FCSTD DOCUMENT  (FreeCAD 0.19R24291 (Git))
Label: Problem06
License: All rights reserved
LicenseURL: http://en.wikipedia.org/wiki/All_rights_reserved
objects: App::FeaturePython×52, Part::Part2DObjectPython×46
note: 46 computed .brp shape members not serialized (recipe doc carries the construction recipe); baked Part::Feature solids carry a one-line shape summary decoded from their .brp

FEATURE [Part::Part2DObjectPython] Polygon  # Draft 2D object (typed FeaturePython)
  Area = 0
  ChamferSize = 0
  DrawMode = 0
  FacesNumber = 5
  FilletRadius = 0
  MakeFace = false
  Placement = pos=(-136.597,-39.2184,0) rot=(0,0,1;0.624663rad)
  Radius = 21.266
FEATURE [Part::Part2DObjectPython] Line004  # Draft 2D object (typed FeaturePython)
  Area = 0
  ChamferSize = 0
  Closed = false
  End = (-119.439,-51.781,0)
  FilletRadius = 0
  Length = 38.4706
  MakeFace = false
  Placement = pos=(-150.479,-29.0549,0) rot=(0,0,1;0rad)
  Points = (2) [(0,0,0),(31.0405,-22.7261,0)]
  Start = (-150.479,-29.0549,0)
  Subdivisions = 0
FEATURE [Part::Part2DObjectPython] Line005  # Draft 2D object (typed FeaturePython)
  Area = 0
  ChamferSize = 0
  Closed = false
  End = (-143.243,-59.4194,0)
  FilletRadius = 0
  Length = 38.4706
  MakeFace = false
  Placement = pos=(-131.221,-22.8754,0) rot=(0,0,1;0rad)
  Points = (2) [(0,0,0),(-12.0217,-36.544,0)]
  Start = (-131.221,-22.8754,0)
  Subdivisions = 0
FEATURE [Part::Part2DObjectPython] Line006  # Draft 2D object (typed FeaturePython)
  Area = 0
  ChamferSize = 0
  Closed = false
  End = (-136.597,-1.42e-14,0)
  FilletRadius = 0
  Length = 39.2184
  MakeFace = false
  Placement = pos=(-136.597,-39.2184,0) rot=(0,0,1;0rad)
  Points = (2) [(0,0,0),(0,39.2184,0)]
  Start = (-136.597,-39.2184,0)
  Subdivisions = 0
FEATURE [Part::Part2DObjectPython] Line007  # Draft 2D object (typed FeaturePython)
  Area = 0
  ChamferSize = 0
  Closed = false
  End = (-136.597,50,0)
  FilletRadius = 0
  Length = 50
  MakeFace = false
  Placement = pos=(-136.597,-1.42e-14,0) rot=(0,0,1;0rad)
  Points = (2) [(0,0,0),(-5.68434e-14,50,0)]
  Start = (-136.597,-1.42e-14,0)
  Subdivisions = 0
FEATURE [Part::Part2DObjectPython] Line009  # Draft 2D object (typed FeaturePython)
  Area = 0
  ChamferSize = 0
  Closed = false
  End = (-157.863,-2.13e-14,0)
  FilletRadius = 0
  Length = 39.1406
  MakeFace = false
  Placement = pos=(-157.863,-39.1406,0) rot=(0,0,1;0rad)
  Points = (2) [(0,0,0),(0,39.1406,0)]
  Start = (-157.863,-39.1406,0)
  Subdivisions = 0
FEATURE [Part::Part2DObjectPython] Line010  # Draft 2D object (typed FeaturePython)
  Area = 0
  ChamferSize = 0
  Closed = false
  End = (-119.347,-1.42e-14,0)
  FilletRadius = 0
  Length = 26.7815
  MakeFace = false
  Placement = pos=(-119.347,-26.7815,0) rot=(0,0,1;0rad)
  Points = (2) [(0,0,0),(0,26.7815,0)]
  Start = (-119.347,-26.7815,0)
  Subdivisions = 0
FEATURE [Part::Part2DObjectPython] Line011  # Draft 2D object (typed FeaturePython)
  Area = 0
  ChamferSize = 0
  Closed = false
  End = (-143.095,-1.78e-14,0)
  FilletRadius = 0
  Length = 18.9693
  MakeFace = false
  Placement = pos=(-143.095,-18.9693,0) rot=(0,0,1;0rad)
  Points = (2) [(0,0,0),(0,18.9693,0)]
  Start = (-143.095,-18.9693,0)
  Subdivisions = 0
FEATURE [Part::Part2DObjectPython] Line013  # Draft 2D object (typed FeaturePython)
  Area = 0
  ChamferSize = 0
  Closed = false
  End = (-157.863,50,0)
  FilletRadius = 0
  Length = 50
  MakeFace = false
  Placement = pos=(-157.863,-2.1e-14,0) rot=(0,0,1;0rad)
  Points = (2) [(0,0,0),(0,50,0)]
  Start = (-157.863,-2.1e-14,0)
  Subdivisions = 0
FEATURE [Part::Part2DObjectPython] Line014  # Draft 2D object (typed FeaturePython)
  Area = 0
  ChamferSize = 0
  Closed = false
  End = (-143.095,50,0)
  FilletRadius = 0
  Length = 50
  MakeFace = false
  Placement = pos=(-143.095,-1.78e-14,0) rot=(0,0,1;0rad)
  Points = (2) [(0,0,0),(-2.84217e-14,50,0)]
  Start = (-143.095,-1.78e-14,0)
  Subdivisions = 0
FEATURE [Part::Part2DObjectPython] Line015  # Draft 2D object (typed FeaturePython)
  Area = 0
  ChamferSize = 0
  Closed = false
  End = (-119.347,50,0)
  FilletRadius = 0
  Length = 50
  MakeFace = false
  Placement = pos=(-119.347,-1.42e-14,0) rot=(0,0,1;0rad)
  Points = (2) [(0,0,0),(-1.42109e-14,50,0)]
  Start = (-119.347,-1.42e-14,0)
  Subdivisions = 0
FEATURE [Part::Part2DObjectPython] Line016  # Draft 2D object (typed FeaturePython)
  Area = 0
  ChamferSize = 0
  Closed = false
  End = (-119.347,50,0)
  FilletRadius = 0
  Length = 38.516
  MakeFace = false
  Placement = pos=(-157.863,50,0) rot=(0,0,1;0rad)
  Points = (2) [(0,0,0),(38.516,0,0)]
  Start = (-157.863,50,0)
  Subdivisions = 0
FEATURE [Part::Part2DObjectPython] Line017  # Draft 2D object (typed FeaturePython)
  Area = 0
  ChamferSize = 0
  Closed = false
  End = (21.0287,62.5593,0)
  FilletRadius = 0
  Length = 50
  MakeFace = false
  Placement = pos=(-3.9713,19.258,0) rot=(0,0,-1;0.523599rad)
  Points = (2) [(0,0,0),(1.77636e-15,50,0)]
  Start = (-3.9713,19.258,0)
  Subdivisions = 0
FEATURE [Part::Part2DObjectPython] Line018  # Draft 2D object (typed FeaturePython)
  Area = 0
  ChamferSize = 0
  Closed = false
  End = (33.8184,55.1751,0)
  FilletRadius = 0
  Length = 50
  MakeFace = false
  Placement = pos=(8.81842,11.8739,0) rot=(0,0,-1;0.523599rad)
  Points = (2) [(0,0,0),(-2.39808e-14,50,0)]
  Start = (8.81842,11.8739,0)
  Subdivisions = 0
FEATURE [Part::Part2DObjectPython] Line019  # Draft 2D object (typed FeaturePython)
  Area = 0
  ChamferSize = 0
  Closed = false
  End = (39.4455,51.9263,0)
  FilletRadius = 0
  Length = 50
  MakeFace = false
  Placement = pos=(14.4455,8.62507,0) rot=(0,0,-1;0.523599rad)
  Points = (2) [(0,0,0),(-3.37508e-14,50,0)]
  Start = (14.4455,8.62507,0)
  Subdivisions = 0
FEATURE [Part::Part2DObjectPython] Line020  # Draft 2D object (typed FeaturePython)
  Area = 0
  ChamferSize = 0
  Closed = false
  End = (54.3845,43.3013,0)
  FilletRadius = 0
  Length = 50
  MakeFace = false
  Placement = pos=(29.3845,4e-15,0) rot=(0,0,-1;0.523599rad)
  Points = (2) [(0,0,0),(-2.13163e-14,50,0)]
  Start = (29.3845,4e-15,0)
  Subdivisions = 0
FEATURE [Part::Part2DObjectPython] Line021  # Draft 2D object (typed FeaturePython)
  Area = 0
  ChamferSize = 0
  Closed = false
  End = (54.3845,43.3013,0)
  FilletRadius = 0
  Length = 38.516
  MakeFace = false
  Placement = pos=(21.0287,62.5593,0) rot=(0,0,-1;0.523599rad)
  Points = (2) [(0,0,0),(38.516,-1.42109e-14,0)]
  Start = (21.0287,62.5593,0)
  Subdivisions = 0
FEATURE [Part::Part2DObjectPython] Line023  # Draft 2D object (typed FeaturePython)
  Area = 0
  ChamferSize = 0
  Closed = false
  End = (-3.9713,19.258,0)
  FilletRadius = 0
  Length = 58.3986
  MakeFace = false
  Placement = pos=(-3.9713,19.258,0) rot=(0,0,1;0rad)
  Points = (2) [(-1.24345e-14,-58.3986,0),(0,0,0)]
  Start = (-3.9713,-39.1406,0)
  Subdivisions = 0
FEATURE [Part::Part2DObjectPython] Line024  # Draft 2D object (typed FeaturePython)
  Area = 0
  ChamferSize = 0
  Closed = false
  End = (8.81842,11.8739,0)
  FilletRadius = 0
  Length = 71.2932
  MakeFace = false
  Placement = pos=(8.81842,11.8739,0) rot=(0,0,1;0rad)
  Points = (2) [(8.88178e-15,-71.2932,0),(0,0,0)]
  Start = (8.81842,-59.4194,0)
  Subdivisions = 0
FEATURE [App::FeaturePython] Text  # WARN: FeaturePython — macro-defined, semantics opaque (R4)
  Placement = pos=(-200.129,1.90969,0) rot=(0,0,1;0rad)
  Text = VP
FEATURE [App::FeaturePython] Text001  # WARN: FeaturePython — macro-defined, semantics opaque (R4)
  Placement = pos=(-200.407,-5.34313,0) rot=(0,0,1;0rad)
  Text = HP
FEATURE [App::FeaturePython] Dimension  # Draft dimension (typed FeaturePython)
  Diameter = false
  Dimline = (-169.104,5.51467,0)
  Direction = (0,0,0)
  Distance = 50
  End = (-157.863,-1.36e-14,0)
  Normal = (0,0,1)
  Start = (-157.863,50,0)
FEATURE [App::FeaturePython] Text002  # WARN: FeaturePython — macro-defined, semantics opaque (R4)
  Placement = pos=(-160.766,50.8523,0) rot=(0,0,1;0rad)
  Text = a'
FEATURE [App::FeaturePython] Text003  # WARN: FeaturePython — macro-defined, semantics opaque (R4)
  Placement = pos=(-162.087,-4.60433,0) rot=(0,0,1;0rad)
  Text = 1'
FEATURE [App::FeaturePython] Text004  # WARN: FeaturePython — macro-defined, semantics opaque (R4)
  Placement = pos=(-146.175,51.3734,0) rot=(0,0,1;0rad)
  Text = b'(e')
FEATURE [App::FeaturePython] Text005  # WARN: FeaturePython — macro-defined, semantics opaque (R4)
  Placement = pos=(-121.421,51.1129,0) rot=(0,0,1;0rad)
  Text = c'(d')
FEATURE [App::FeaturePython] Text006  # WARN: FeaturePython — macro-defined, semantics opaque (R4)
  Placement = pos=(-147.477,-4.90778,0) rot=(0,0,1;0rad)
  Text = 2'(5')
FEATURE [App::FeaturePython] Text007  # WARN: FeaturePython — macro-defined, semantics opaque (R4)
  Placement = pos=(-123.506,-4.64722,0) rot=(0,0,1;0rad)
  Text = 3'(4')
FEATURE [App::FeaturePython] Text008  # WARN: FeaturePython — macro-defined, semantics opaque (R4)
  Placement = pos=(-167.801,-38.7807,0) rot=(0,0,1;0rad)
  Text = a(1)
FEATURE [App::FeaturePython] Text009  # WARN: FeaturePython — macro-defined, semantics opaque (R4)
  Placement = pos=(-143.83,-65.0974,0) rot=(0,0,1;0rad)
  Text = b(2)
FEATURE [App::FeaturePython] Text010  # WARN: FeaturePython — macro-defined, semantics opaque (R4)
  Placement = pos=(-118.555,-50.7665,0) rot=(0,0,1;0rad)
  Text = c(3)
FEATURE [App::FeaturePython] Text011  # WARN: FeaturePython — macro-defined, semantics opaque (R4)
  Placement = pos=(-117.513,-25.7527,0) rot=(0,0,1;0rad)
  Text = d(4)
FEATURE [App::FeaturePython] Text012  # WARN: FeaturePython — macro-defined, semantics opaque (R4)
  Placement = pos=(-142.787,-17.4147,0) rot=(0,0,1;0rad)
  Text = e(5)
FEATURE [App::FeaturePython] Dimension001  # Draft dimension (typed FeaturePython)
  Diameter = false
  Dimline = (-151.386,-63.0129,0)
  Direction = (0,0,0)
  Distance = 24.9997
  End = (-143.243,-59.4194,0)
  Normal = (0,0,1)
  Start = (-157.863,-39.1406,0)
FEATURE [Part::Part2DObjectPython] Line027  # Draft 2D object (typed FeaturePython)
  Area = 0
  ChamferSize = 0
  Closed = false
  End = (-143.095,-18.9693,0)
  FilletRadius = 0
  Length = 223.348
  MakeFace = false
  Placement = pos=(-143.095,-18.9693,0) rot=(0,0,1;0rad)
  Points = (2) [(223.348,-2.4869e-14,0),(0,0,0)]
  Start = (80.253,-18.9693,0)
  Subdivisions = 0
FEATURE [Part::Part2DObjectPython] Line028  # Draft 2D object (typed FeaturePython)
  Area = 0
  ChamferSize = 0
  Closed = false
  End = (-157.863,-39.1406,0)
  FilletRadius = 0
  Length = 238.116
  MakeFace = false
  Placement = pos=(-157.863,-39.1406,0) rot=(0,0,1;0rad)
  Points = (2) [(238.116,-3.55271e-14,0),(0,0,0)]
  Start = (80.253,-39.1406,0)
  Subdivisions = 0
FEATURE [Part::Part2DObjectPython] Line029  # Draft 2D object (typed FeaturePython)
  Area = 0
  ChamferSize = 0
  Closed = false
  End = (-143.243,-59.4194,0)
  FilletRadius = 0
  Length = 223.496
  MakeFace = false
  Placement = pos=(-143.243,-59.4194,0) rot=(0,0,1;0rad)
  Points = (2) [(223.496,-4.26326e-14,0),(0,0,0)]
  Start = (80.253,-59.4194,0)
  Subdivisions = 0
FEATURE [Part::Part2DObjectPython] Line030  # Draft 2D object (typed FeaturePython)
  Area = 0
  ChamferSize = 0
  Closed = false
  End = (-119.347,-26.7815,0)
  FilletRadius = 0
  Length = 199.6
  MakeFace = false
  Placement = pos=(-119.347,-26.7815,0) rot=(0,0,1;0rad)
  Points = (2) [(199.6,-7.10543e-15,0),(0,0,0)]
  Start = (80.253,-26.7815,0)
  Subdivisions = 0
FEATURE [Part::Part2DObjectPython] Line031  # Draft 2D object (typed FeaturePython)
  Area = 0
  ChamferSize = 0
  Closed = false
  End = (-119.439,-51.781,0)
  FilletRadius = 0
  Length = 199.692
  MakeFace = false
  Placement = pos=(-119.439,-51.781,0) rot=(0,0,1;0rad)
  Points = (2) [(199.692,-6.39488e-14,0),(0,0,0)]
  Start = (80.253,-51.781,0)
  Subdivisions = 0
FEATURE [Part::Part2DObjectPython] Line032  # Draft 2D object (typed FeaturePython)
  Area = 0
  ChamferSize = 0
  Closed = false
  End = (21.0287,62.5593,0)
  FilletRadius = 0
  Length = 101.7
  MakeFace = false
  Placement = pos=(21.0287,62.5593,0) rot=(0,0,1;0rad)
  Points = (2) [(-1.06581e-14,-101.7,0),(0,0,0)]
  Start = (21.0287,-39.1406,0)
  Subdivisions = 0
FEATURE [Part::Part2DObjectPython] Line033  # Draft 2D object (typed FeaturePython)
  Area = 0
  ChamferSize = 0
  Closed = false
  End = (33.8184,55.1751,0)
  FilletRadius = 0
  Length = 114.594
  MakeFace = false
  Placement = pos=(33.8184,55.1751,0) rot=(0,0,1;0rad)
  Points = (2) [(0,-114.594,0),(0,0,0)]
  Start = (33.8184,-59.4194,0)
  Subdivisions = 0
FEATURE [App::FeaturePython] Text013  # WARN: FeaturePython — macro-defined, semantics opaque (R4)
  Placement = pos=(-7.59819,-37.5917,0) rot=(0,0,1;0rad)
  Text = 1
FEATURE [App::FeaturePython] Text014  # WARN: FeaturePython — macro-defined, semantics opaque (R4)
  Placement = pos=(-5.71338,-38.0629,0) rot=(0,0,1;0rad)
  Text = 1
FEATURE [App::FeaturePython] Text015  # WARN: FeaturePython — macro-defined, semantics opaque (R4)
  Placement = pos=(4.02486,-17.9582,0) rot=(0,0,1;0rad)
  Text = 5
FEATURE [App::FeaturePython] Text016  # WARN: FeaturePython — macro-defined, semantics opaque (R4)
  Placement = pos=(19.2582,-42.6379,0) rot=(0,0,1;0rad)
  Text = a
FEATURE [App::FeaturePython] Text017  # WARN: FeaturePython — macro-defined, semantics opaque (R4)
  Placement = pos=(9.52225,-64.1363,0) rot=(0,0,1;0rad)
  Text = 2
FEATURE [App::FeaturePython] Text018  # WARN: FeaturePython — macro-defined, semantics opaque (R4)
  Placement = pos=(29.9411,-30.5237,0) rot=(0,0,1;0rad)
  Text = 4
FEATURE [App::FeaturePython] Text019  # WARN: FeaturePython — macro-defined, semantics opaque (R4)
  Placement = pos=(29.1558,-49.8431,0) rot=(0,0,1;0rad)
  Text = 3
FEATURE [App::FeaturePython] Text020  # WARN: FeaturePython — macro-defined, semantics opaque (R4)
  Placement = pos=(6.53796,-17.9582,0) rot=(0,0,1;0rad)
  Text = 1
FEATURE [App::FeaturePython] Text021  # WARN: FeaturePython — macro-defined, semantics opaque (R4)
  Placement = pos=(32.2972,-31.309,0) rot=(0,0,1;0rad)
  Text = 1
FEATURE [App::FeaturePython] Text022  # WARN: FeaturePython — macro-defined, semantics opaque (R4)
  Placement = pos=(31.8269,-50.0418,0) rot=(0,0,1;0rad)
  Text = 1
FEATURE [App::FeaturePython] Text023  # WARN: FeaturePython — macro-defined, semantics opaque (R4)
  Placement = pos=(12.9787,-64.4921,0) rot=(0,0,1;0rad)
  Text = 1
FEATURE [App::FeaturePython] Text024  # WARN: FeaturePython — macro-defined, semantics opaque (R4)
  Placement = pos=(55.3862,-30.2235,0) rot=(0,0,1;0rad)
  Text = d
FEATURE [App::FeaturePython] Text025  # WARN: FeaturePython — macro-defined, semantics opaque (R4)
  Placement = pos=(55.2291,-50.6423,0) rot=(0,0,1;0rad)
  Text = c
FEATURE [App::FeaturePython] Text026  # WARN: FeaturePython — macro-defined, semantics opaque (R4)
  Placement = pos=(34.9729,-17.9378,0) rot=(0,0,1;0rad)
  Text = e
FEATURE [App::FeaturePython] Text027  # WARN: FeaturePython — macro-defined, semantics opaque (R4)
  Placement = pos=(34.6588,-62.8593,0) rot=(0,0,1;0rad)
  Text = b
FEATURE [App::FeaturePython] Text028  # WARN: FeaturePython — macro-defined, semantics opaque (R4)
  Placement = pos=(37.3233,-18.2723,0) rot=(0,0,1;0rad)
  Text = 1
FEATURE [App::FeaturePython] Text029  # WARN: FeaturePython — macro-defined, semantics opaque (R4)
  Placement = pos=(58.0564,-30.9949,0) rot=(0,0,1;0rad)
  Text = 1
FEATURE [App::FeaturePython] Text030  # WARN: FeaturePython — macro-defined, semantics opaque (R4)
  Placement = pos=(57.7422,-51.2567,0) rot=(0,0,1;0rad)
  Text = 1
FEATURE [Part::Part2DObjectPython] Line036  # Draft 2D object (typed FeaturePython)
  Area = 0
  ChamferSize = 0
  Closed = false
  End = (8.81842,-18.9693,0)
  FilletRadius = 0
  Length = 23.8843
  MakeFace = false
  Placement = pos=(-3.9713,-39.1406,0) rot=(0,0,1;0rad)
  Points = (2) [(0,0,0),(12.7897,20.1713,0)]
  Start = (-3.9713,-39.1406,0)
  Subdivisions = 0
FEATURE [Part::Part2DObjectPython] Line037  # Draft 2D object (typed FeaturePython)
  Area = 0
  ChamferSize = 0
  Closed = false
  End = (8.81842,-59.4194,0)
  FilletRadius = 0
  Length = 23.9751
  MakeFace = false
  Placement = pos=(-3.9713,-39.1406,0) rot=(0,0,1;0rad)
  Points = (2) [(0,0,0),(12.7897,-20.2788,0)]
  Start = (-3.9713,-39.1406,0)
  Subdivisions = 0
FEATURE [Part::Part2DObjectPython] Line038  # Draft 2D object (typed FeaturePython)
  Area = 0
  ChamferSize = 0
  Closed = false
  End = (29.3845,-59.4194,0)
  FilletRadius = 0
  Length = 59.4194
  MakeFace = false
  Placement = pos=(29.3845,7.1e-15,0) rot=(0,0,1;0rad)
  Points = (2) [(0,0,0),(-1.42109e-14,-59.4194,0)]
  Start = (29.3845,7.1e-15,0)
  Subdivisions = 0
FEATURE [Part::Part2DObjectPython] Line039  # Draft 2D object (typed FeaturePython)
  Area = 0
  ChamferSize = 0
  Closed = false
  End = (29.3845,-26.7815,0)
  FilletRadius = 0
  Length = 21.9999
  MakeFace = false
  Placement = pos=(8.81842,-18.9693,0) rot=(0,0,1;0rad)
  Points = (2) [(0,0,0),(20.5661,-7.8122,0)]
  Start = (8.81842,-18.9693,0)
  Subdivisions = 0
FEATURE [Part::Part2DObjectPython] Line040  # Draft 2D object (typed FeaturePython)
  Area = 0
  ChamferSize = 0
  Closed = false
  End = (29.3845,-51.781,0)
  FilletRadius = 0
  Length = 21.9388
  MakeFace = false
  Placement = pos=(8.81842,-59.4194,0) rot=(0,0,1;0rad)
  Points = (2) [(0,0,0),(20.5661,7.63835,0)]
  Start = (8.81842,-59.4194,0)
  Subdivisions = 0
FEATURE [Part::Part2DObjectPython] Line041  # Draft 2D object (typed FeaturePython)
  Area = 0
  ChamferSize = 0
  Closed = false
  End = (29.3845,-51.781,0)
  FilletRadius = 0
  Length = 24.9995
  MakeFace = false
  Placement = pos=(29.3845,-26.7815,0) rot=(0,0,1;0rad)
  Points = (2) [(0,0,0),(0,-24.9995,0)]
  Start = (29.3845,-26.7815,0)
  Subdivisions = 0
FEATURE [Part::Part2DObjectPython] Line042  # Draft 2D object (typed FeaturePython)
  Area = 0
  ChamferSize = 0
  Closed = false
  End = (54.3845,-51.781,0)
  FilletRadius = 0
  Length = 21.9388
  MakeFace = false
  Placement = pos=(33.8184,-59.4194,0) rot=(0,0,1;0rad)
  Points = (2) [(0,0,0),(20.5661,7.63835,0)]
  Start = (33.8184,-59.4194,0)
  Subdivisions = 0
FEATURE [Part::Part2DObjectPython] Line043  # Draft 2D object (typed FeaturePython)
  Area = 0
  ChamferSize = 0
  Closed = false
  End = (33.8184,-59.4194,0)
  FilletRadius = 0
  Length = 23.9751
  MakeFace = false
  Placement = pos=(21.0287,-39.1406,0) rot=(0,0,1;0rad)
  Points = (2) [(0,0,0),(12.7897,-20.2788,0)]
  Start = (21.0287,-39.1406,0)
  Subdivisions = 0
FEATURE [Part::Part2DObjectPython] Line044  # Draft 2D object (typed FeaturePython)
  Area = 0
  ChamferSize = 0
  Closed = false
  End = (33.8184,-18.9693,0)
  FilletRadius = 0
  Length = 23.8843
  MakeFace = false
  Placement = pos=(21.0287,-39.1406,0) rot=(0,0,1;0rad)
  Points = (2) [(0,0,0),(12.7897,20.1713,0)]
  Start = (21.0287,-39.1406,0)
  Subdivisions = 0
FEATURE [Part::Part2DObjectPython] Line045  # Draft 2D object (typed FeaturePython)
  Area = 0
  ChamferSize = 0
  Closed = false
  End = (54.3845,-26.7815,0)
  FilletRadius = 0
  Length = 21.9999
  MakeFace = false
  Placement = pos=(33.8184,-18.9693,0) rot=(0,0,1;0rad)
  Points = (2) [(0,0,0),(20.5661,-7.8122,0)]
  Start = (33.8184,-18.9693,0)
  Subdivisions = 0
FEATURE [Part::Part2DObjectPython] Line046  # Draft 2D object (typed FeaturePython)
  Area = 0
  ChamferSize = 0
  Closed = false
  End = (54.3845,-51.781,0)
  FilletRadius = 0
  Length = 24.9995
  MakeFace = false
  Placement = pos=(54.3845,-26.7815,0) rot=(0,0,1;0rad)
  Points = (2) [(0,0,0),(0,-24.9995,0)]
  Start = (54.3845,-26.7815,0)
  Subdivisions = 0
FEATURE [Part::Part2DObjectPython] Line035  # Draft 2D object (typed FeaturePython)
  Area = 0
  ChamferSize = 0
  Closed = false
  End = (54.3845,43.3013,0)
  FilletRadius = 0
  Length = 95.0823
  MakeFace = false
  Placement = pos=(54.3845,43.3013,0) rot=(0,0,1;0rad)
  Points = (2) [(-4.9738e-14,-95.0823,0),(0,0,0)]
  Start = (54.3845,-51.781,0)
  Subdivisions = 0
FEATURE [Part::Part2DObjectPython] Line047  # Draft 2D object (typed FeaturePython)
  Area = 0
  ChamferSize = 0
  Closed = false
  End = (33.8184,-18.9693,0)
  FilletRadius = 0
  Length = 25
  MakeFace = false
  Placement = pos=(8.81842,-18.9693,0) rot=(0,0,1;0rad)
  Points = (2) [(0,0,0),(25,-1.06581e-14,0)]
  Start = (8.81842,-18.9693,0)
  Subdivisions = 0
FEATURE [Part::Part2DObjectPython] Line048  # Draft 2D object (typed FeaturePython)
  Area = 0
  ChamferSize = 0
  Closed = false
  End = (21.0287,-39.1406,0)
  FilletRadius = 0
  Length = 25
  MakeFace = false
  Placement = pos=(-3.9713,-39.1406,0) rot=(0,0,1;0rad)
  Points = (2) [(0,0,0),(25,-7.10543e-15,0)]
  Start = (-3.9713,-39.1406,0)
  Subdivisions = 0
FEATURE [Part::Part2DObjectPython] Line049  # Draft 2D object (typed FeaturePython)
  Area = 0
  ChamferSize = 0
  Closed = false
  End = (54.3845,-26.7815,0)
  FilletRadius = 0
  Length = 25
  MakeFace = false
  Placement = pos=(29.3845,-26.7815,0) rot=(0,0,1;0rad)
  Points = (2) [(0,0,0),(25,-7.10543e-15,0)]
  Start = (29.3845,-26.7815,0)
  Subdivisions = 0
FEATURE [Part::Part2DObjectPython] Line050  # Draft 2D object (typed FeaturePython)
  Area = 0
  ChamferSize = 0
  Closed = false
  End = (54.3845,-51.781,0)
  FilletRadius = 0
  Length = 25
  MakeFace = false
  Placement = pos=(29.3845,-51.781,0) rot=(0,0,1;0rad)
  Points = (2) [(0,0,0),(25,-7.10543e-15,0)]
  Start = (29.3845,-51.781,0)
  Subdivisions = 0
FEATURE [Part::Part2DObjectPython] Line051  # Draft 2D object (typed FeaturePython)
  Area = 0
  ChamferSize = 0
  Closed = false
  End = (33.8184,-59.4194,0)
  FilletRadius = 0
  Length = 25
  MakeFace = false
  Placement = pos=(8.81842,-59.4194,0) rot=(0,0,1;0rad)
  Points = (2) [(0,0,0),(25,-7.10543e-15,0)]
  Start = (8.81842,-59.4194,0)
  Subdivisions = 0
FEATURE [App::FeaturePython] Text032  # WARN: FeaturePython — macro-defined, semantics opaque (R4)
  Placement = pos=(-8.41329,18.4223,0) rot=(0,0,1;0rad)
  Text = 1'
FEATURE [App::FeaturePython] Text033  # WARN: FeaturePython — macro-defined, semantics opaque (R4)
  Placement = pos=(20.6967,63.3945,0) rot=(0,0,1;0rad)
  Text = a'
FEATURE [App::FeaturePython] Text034  # WARN: FeaturePython — macro-defined, semantics opaque (R4)
  Placement = pos=(33.2471,56.0735,0) rot=(0,0,1;0rad)
  Text = b'(e')
FEATURE [App::FeaturePython] Text035  # WARN: FeaturePython — macro-defined, semantics opaque (R4)
  Placement = pos=(54.513,44.046,0) rot=(0,0,1;0rad)
  Text = c'(d')
FEATURE [App::FeaturePython] Text036  # WARN: FeaturePython — macro-defined, semantics opaque (R4)
  Placement = pos=(-1.78947,7.7893,0) rot=(0,0,1;0rad)
  Text = 2'(5')
FEATURE [App::FeaturePython] Text037  # WARN: FeaturePython — macro-defined, semantics opaque (R4)
  Placement = pos=(32.4932,0.72688,0) rot=(0,0,1;0rad)
  Text = 3'(4')
FEATURE [Part::Part2DObjectPython] Line052  # Draft 2D object (typed FeaturePython)
  Area = 0
  ChamferSize = 0
  Closed = false
  End = (-119.347,-1.51e-14,0)
  FilletRadius = 0
  Length = 38.516
  MakeFace = false
  Placement = pos=(-157.863,-2.1e-14,0) rot=(0,0,1;0rad)
  Points = (2) [(0,0,0),(38.516,5.92622e-15,0)]
  Start = (-157.863,-2.1e-14,0)
  Subdivisions = 0
FEATURE [App::FeaturePython] Text038  # WARN: FeaturePython — macro-defined, semantics opaque (R4)
  Placement = pos=(-207.006,-1.36502,0) rot=(0,0,1;0rad)
  Text = X
FEATURE [App::FeaturePython] Text039  # WARN: FeaturePython — macro-defined, semantics opaque (R4)
  Placement = pos=(87.7729,-0.696078,0) rot=(0,0,1;0rad)
  Text = Y
FEATURE [Part::Part2DObjectPython] Line  # Draft 2D object (typed FeaturePython)
  Area = 0
  ChamferSize = 0
  Closed = false
  End = (85.79,0.0497156,0)
  FilletRadius = 0
  Length = 287.74
  MakeFace = false
  Placement = pos=(85.79,0.0497156,0) rot=(0,0,1;0rad)
  Points = (2) [(-287.74,-0.0587113,0),(0,0,0)]
  Start = (-201.95,-0.00899567,0)
  Subdivisions = 0
FEATURE [App::FeaturePython] Text040  # WARN: FeaturePython — macro-defined, semantics opaque (R4)
  Placement = pos=(-156.163,-87.135,0) rot=(0,0,1;0rad)
  Text = FIRST TOP VIEW
FEATURE [App::FeaturePython] Text041  # WARN: FeaturePython — macro-defined, semantics opaque (R4)
  Placement = pos=(4.05342,-87.135,0) rot=(0,0,1;0rad)
  Text = FINAL TOP VIEW
FEATURE [App::FeaturePython] Text042  # WARN: FeaturePython — macro-defined, semantics opaque (R4)
  Placement = pos=(-160.247,79.3641,0) rot=(0,0,1;0rad)
  Text = FIRST FRONT VIEW
FEATURE [App::FeaturePython] Text043  # WARN: FeaturePython — macro-defined, semantics opaque (R4)
  Placement = pos=(3.42512,77.7934,0) rot=(0,0,1;0rad)
  Text = FINAL FRONT VIEW
FEATURE [App::FeaturePython] Text044  # WARN: FeaturePython — macro-defined, semantics opaque (R4)
  Placement = pos=(-139.513,-80.5379,0) rot=(0,0,1;0rad)
  Text = I
FEATURE [App::FeaturePython] Text045  # WARN: FeaturePython — macro-defined, semantics opaque (R4)
  Placement = pos=(-141.084,86.9037,0) rot=(0,0,1;0rad)
  Text = II
FEATURE [App::FeaturePython] Text046  # WARN: FeaturePython — macro-defined, semantics opaque (R4)
  Placement = pos=(17.5618,86.9037,0) rot=(0,0,1;0rad)
  Text = III
FEATURE [App::FeaturePython] Text047  # WARN: FeaturePython — macro-defined, semantics opaque (R4)
  Placement = pos=(20.7033,-78.3388,0) rot=(0,0,1;0rad)
  Text = IV
FEATURE [App::FeaturePython] Text048  # WARN: FeaturePython — macro-defined, semantics opaque (R4)
  Placement = pos=(-80.4724,-95.6714,0) rot=(0,0,1;0rad)
  Text = All Dimensions are in 'mm'
FEATURE [Part::Part2DObjectPython] Line022  # Draft 2D object (typed FeaturePython)
  Area = 0
  ChamferSize = 0
  Closed = false
  End = (29.3845,7.1e-15,0)
  FilletRadius = 0
  Length = 38.516
  MakeFace = false
  Placement = pos=(-3.9713,19.258,0) rot=(0,0,1;0rad)
  Points = (2) [(0,0,0),(33.3558,-19.258,0)]
  Start = (-3.9713,19.258,0)
  Subdivisions = 0
FEATURE [App::FeaturePython] Dimension002  # Draft dimension (typed FeaturePython)
  Angle = 30.0117
  Center = (29.3184,0.038193,0)
  Dimline = (13.7848,4.50917,0)
  FirstAngle = 150
  LastAngle = 180.012
  Normal = (0,0,1)
FEATURE [App::FeaturePython] Text049  # WARN: FeaturePython — macro-defined, semantics opaque (R4)
  Placement = pos=(36.8773,-63.5859,0) rot=(0,0,1;0rad)
  Text = 1
